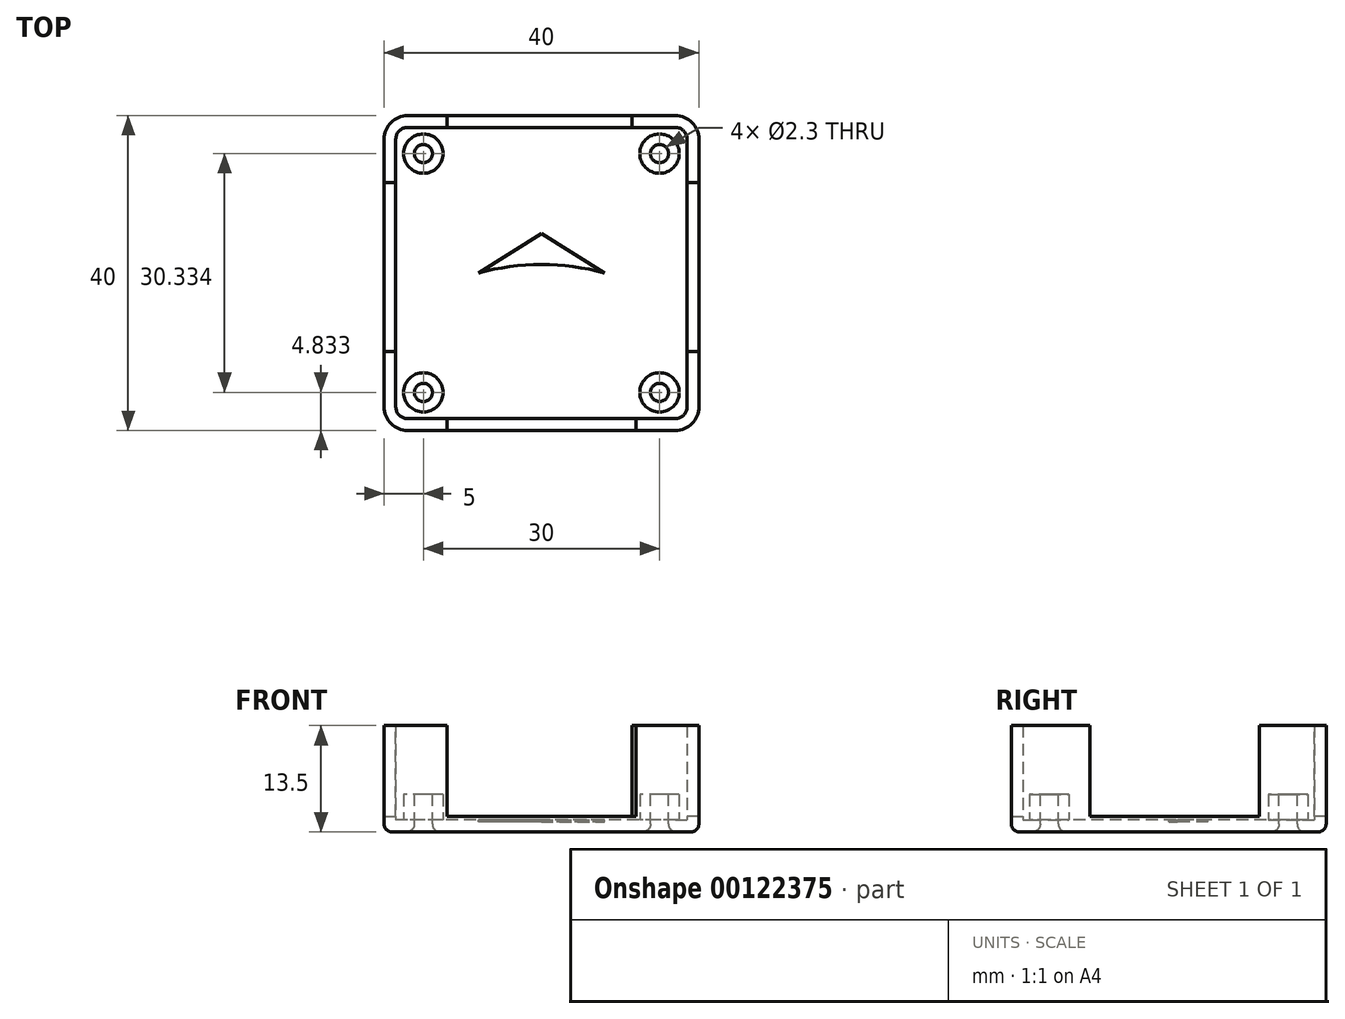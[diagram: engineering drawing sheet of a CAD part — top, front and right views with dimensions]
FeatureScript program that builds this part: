
annotation { "Feature Type Name" : "Feature", "Feature Type Description" : "" }
export const myFeature = defineFeature(function(context is Context, id is Id, definition is map)
    precondition{}
    {
        {
            var Q0;
            Q0=qCreatedBy(makeId("Top.planeOp"),FACE);
            var sketch = newSketch(context, id + "F0", { "sketchPlane" : qUnion([Q0])});
            skLineSegment(sketch, "E0.bottom", {"start": v(20, 20) * mm, "end": v(-20, 20) * mm});
            skLineSegment(sketch, "E0.top", {"start": v(20, -20) * mm, "end": v(-20, -20) * mm});
            skLineSegment(sketch, "E0.left", {"start": v(20, 20) * mm, "end": v(20, -20) * mm});
            skLineSegment(sketch, "E0.right", {"start": v(-20, 20) * mm, "end": v(-20, -20) * mm});
            skPoint(sketch, "E0.middle", {"position": v(0, 0) * mm});
            skSolve(sketch);
        }
        {
            var Q0;
            Q0 = qSketchRegion(id + "F0", true);
            extrude(context, id + "F1", {"entities" : qUnion([Q0]), "depth" : 1.5 * mm});
        }
        {
            var Q0;
            Q0=makeQuery(id+"F1.opExtrude","CAP_FACE",FACE,{"disambiguationData":[OSD([sQuery(id+"F0.wireOp",EDGE,"E0.bottom"),sQuery(id+"F0.wireOp",EDGE,"E0.top"),sQuery(id+"F0.wireOp",EDGE,"E0.left"),sQuery(id+"F0.wireOp",EDGE,"E0.right")])],"isStart":false});
            var sketch = newSketch(context, id + "F2", { "sketchPlane" : qUnion([Q0])});
            skLineSegment(sketch, "E1.0", {"start": v(20, 20) * mm, "end": v(-20, 20) * mm});
            skLineSegment(sketch, "E2.0", {"start": v(-20, 20) * mm, "end": v(-20, -20) * mm});
            skLineSegment(sketch, "E3.0", {"start": v(20, 20) * mm, "end": v(20, -20) * mm});
            skLineSegment(sketch, "E4.0", {"start": v(20, -20) * mm, "end": v(-20, -20) * mm});
            skLineSegment(sketch, "E5.0", {"start": v(18.5, 18.5) * mm, "end": v(-18.5, 18.5) * mm});
            skLineSegment(sketch, "E6.0", {"start": v(-18.5, 18.5) * mm, "end": v(-18.5, -18.5) * mm});
            skLineSegment(sketch, "E7.0", {"start": v(18.5, -18.5) * mm, "end": v(-18.5, -18.5) * mm});
            skLineSegment(sketch, "E8.0", {"start": v(18.5, 18.5) * mm, "end": v(18.5, -18.5) * mm});
            skSolve(sketch);
        }
        {
            var Q0;
            Q0 = qSketchRegion(id + "F2", true);
            extrude(context, id + "F3", {"entities" : qUnion([Q0]), "operationType" : NewBodyOperationType.ADD, "depth" : 12 * mm});
        }
        {
            var Q0;
            Q0=makeQuery(id+"F1.opExtrude","CAP_FACE",FACE,{"disambiguationData":[OSD([sQuery(id+"F0.wireOp",EDGE,"E0.bottom"),sQuery(id+"F0.wireOp",EDGE,"E0.top"),sQuery(id+"F0.wireOp",EDGE,"E0.left"),sQuery(id+"F0.wireOp",EDGE,"E0.right")])],"isStart":false});
            var sketch = newSketch(context, id + "F4", { "sketchPlane" : qUnion([Q0])});
            skLineSegment(sketch, "E9.bottom", {"start": v(15, -15.17) * mm, "end": v(-15, -15.17) * mm, "construction": true});
            skLineSegment(sketch, "E9.top", {"start": v(15, 15.17) * mm, "end": v(-15, 15.17) * mm, "construction": true});
            skLineSegment(sketch, "E9.left", {"start": v(15, -15.17) * mm, "end": v(15, 15.17) * mm, "construction": true});
            skLineSegment(sketch, "E9.right", {"start": v(-15, -15.17) * mm, "end": v(-15, 15.17) * mm, "construction": true});
            skPoint(sketch, "E9.middle", {"position": v(0, 0) * mm});
            skCircle(sketch, "E10", {"center": v(-15, 15.17) * mm, "radius": 2.5 * mm});
            skCircle(sketch, "E11", {"center": v(15, 15.17) * mm, "radius": 2.5 * mm});
            skCircle(sketch, "E12", {"center": v(15, -15.17) * mm, "radius": 2.5 * mm});
            skCircle(sketch, "E13", {"center": v(-15, -15.17) * mm, "radius": 2.5 * mm});
            skSolve(sketch);
        }
        {
            var Q0;
            Q0 = qSketchRegion(id + "F4", true);
            extrude(context, id + "F5", {"entities" : qUnion([Q0]), "operationType" : NewBodyOperationType.ADD, "depth" : 3.25 * mm});
        }
        {
            var Q0;
            Q0=makeQuery(id+"F5.opExtrude","CAP_FACE",FACE,{"disambiguationData":[OSD([sQuery(id+"F4.wireOp",EDGE,"E10")])],"isStart":false});
            var sketch = newSketch(context, id + "F6", { "sketchPlane" : qUnion([Q0])});
            skCircle(sketch, "E14", {"center": v(-15, 15.17) * mm, "radius": 1.15 * mm});
            skCircle(sketch, "E15.0", {"center": v(15, 15.17) * mm, "radius": 2.5 * mm, "construction": true});
            skCircle(sketch, "E16.1", {"center": v(-15, -15.17) * mm, "radius": 2.5 * mm, "construction": true});
            skCircle(sketch, "E16.2", {"center": v(15, -15.17) * mm, "radius": 2.5 * mm, "construction": true});
            skCircle(sketch, "E17", {"center": v(15, 15.17) * mm, "radius": 1.15 * mm});
            skCircle(sketch, "E18", {"center": v(-15, -15.17) * mm, "radius": 1.15 * mm});
            skCircle(sketch, "E19", {"center": v(15, -15.17) * mm, "radius": 1.15 * mm});
            skSolve(sketch);
        }
        {
            var Q0;
            Q0 = qSketchRegion(id + "F6", true);
            extrude(context, id + "F7", {"entities" : qUnion([Q0]), "operationType" : NewBodyOperationType.REMOVE, "endBound" : BoundingType.THROUGH_ALL, "oppositeDirection" : true, "depth" : 25.4 * mm});
        }
        {
            var Q0;
            Q0=makeQuery(id+"F3.opExtrude","CAP_FACE",FACE,{"disambiguationData":[OSD([sQuery(id+"F2.wireOp",EDGE,"E1.0"),sQuery(id+"F2.wireOp",EDGE,"E2.0"),sQuery(id+"F2.wireOp",EDGE,"E3.0"),sQuery(id+"F2.wireOp",EDGE,"E4.0"),sQuery(id+"F2.wireOp",EDGE,"E5.0"),sQuery(id+"F2.wireOp",EDGE,"E6.0"),sQuery(id+"F2.wireOp",EDGE,"E7.0"),sQuery(id+"F2.wireOp",EDGE,"E8.0")])],"isStart":false});
            var sketch = newSketch(context, id + "F8", { "sketchPlane" : qUnion([Q0])});
            skLineSegment(sketch, "E20", {"start": v(-12, 25.4) * mm, "end": v(-12, 11.5) * mm});
            skLineSegment(sketch, "E21", {"start": v(-12, 11.5) * mm, "end": v(-27.13, 11.5) * mm});
            skLineSegment(sketch, "E22", {"start": v(-27.13, 11.5) * mm, "end": v(-27.13, -10) * mm});
            skLineSegment(sketch, "E23", {"start": v(-27.13, -10) * mm, "end": v(-12, -10) * mm});
            skLineSegment(sketch, "E24", {"start": v(-12, -10) * mm, "end": v(-12, -25.4) * mm});
            skLineSegment(sketch, "E25", {"start": v(-12, -25.4) * mm, "end": v(12, -25.4) * mm});
            skLineSegment(sketch, "E26", {"start": v(12, -25.4) * mm, "end": v(12, -10) * mm});
            skLineSegment(sketch, "E27", {"start": v(12, -10) * mm, "end": v(25.4, -10) * mm});
            skLineSegment(sketch, "E28", {"start": v(25.4, -10) * mm, "end": v(25.4, 11.5) * mm});
            skLineSegment(sketch, "E29", {"start": v(25.4, 11.5) * mm, "end": v(11.5, 11.5) * mm});
            skLineSegment(sketch, "E30", {"start": v(11.5, 11.5) * mm, "end": v(11.5, 25.4) * mm});
            skLineSegment(sketch, "E31", {"start": v(11.5, 25.4) * mm, "end": v(-12, 25.4) * mm});
            skSolve(sketch);
        }
        {
            var Q0;
            Q0 = qSketchRegion(id + "F8", true);
            extrude(context, id + "F9", {"entities" : qUnion([Q0]), "operationType" : NewBodyOperationType.REMOVE, "oppositeDirection" : true, "depth" : 11.5 * mm});
        }
        {
            var Q0;
            Q0=makeQuery(id+"F1.opExtrude","CAP_FACE",FACE,{"disambiguationData":[OSD([sQuery(id+"F0.wireOp",EDGE,"E0.bottom"),sQuery(id+"F0.wireOp",EDGE,"E0.top"),sQuery(id+"F0.wireOp",EDGE,"E0.left"),sQuery(id+"F0.wireOp",EDGE,"E0.right")])],"isStart":false});
            var sketch = newSketch(context, id + "F10", { "sketchPlane" : qUnion([Q0])});
            skLineSegment(sketch, "E32", {"start": v(0, 0) * mm, "end": v(0, 10) * mm, "construction": true});
            skLineSegment(sketch, "E33", {"start": v(0, 5) * mm, "end": v(-8, 0) * mm});
            skLineSegment(sketch, "E34", {"start": v(0, 5) * mm, "end": v(8, 0) * mm});
            skArc(sketch, "E35", {"start": v(8, 0) * mm, "mid": v(0, 1.09) * mm, "end": v(-8, 0) * mm});
            skSolve(sketch);
        }
        {
            var Q0;
            Q0 = qSketchRegion(id + "F10", true);
            extrude(context, id + "F11", {"entities" : qUnion([Q0]), "operationType" : NewBodyOperationType.REMOVE, "oppositeDirection" : true, "depth" : .25 * mm});
        }
        {
            var Q0;
            Q0=makeQuery(id+"F1.opExtrude","CAP_FACE",FACE,{"disambiguationData":[OSD([sQuery(id+"F0.wireOp",EDGE,"E0.bottom"),sQuery(id+"F0.wireOp",EDGE,"E0.top"),sQuery(id+"F0.wireOp",EDGE,"E0.left"),sQuery(id+"F0.wireOp",EDGE,"E0.right")])],"isStart":true});
            fillet(context, id + "F12", {"entities" : qUnion([Q0]), "radius" : 1 * mm, "tangentPropagation" : true, "allowEdgeOverflow" : false});
        }
        {
            var Q0;
            Q0=makeQuery(id+"F3.boolean.opBoolean","MERGE",EDGE,{"derivedFrom":[makeQuery(id+"F1.opExtrude","SWEPT_EDGE",EDGE,{"disambiguationData":[OSD([sQuery(id+"F0.wireOp",EDGE,"E0.top"),sQuery(id+"F0.wireOp",EDGE,"E0.left")])]}),makeQuery(id+"F3.opExtrude","SWEPT_EDGE",EDGE,{"disambiguationData":[OSD([sQuery(id+"F2.wireOp",EDGE,"E3.0"),sQuery(id+"F2.wireOp",EDGE,"E4.0")])]})]});
            var Q1;
            Q1=makeQuery(id+"F3.boolean.opBoolean","MERGE",EDGE,{"derivedFrom":[makeQuery(id+"F1.opExtrude","SWEPT_EDGE",EDGE,{"disambiguationData":[OSD([sQuery(id+"F0.wireOp",EDGE,"E0.bottom"),sQuery(id+"F0.wireOp",EDGE,"E0.left")])]}),makeQuery(id+"F3.opExtrude","SWEPT_EDGE",EDGE,{"disambiguationData":[OSD([sQuery(id+"F2.wireOp",EDGE,"E1.0"),sQuery(id+"F2.wireOp",EDGE,"E3.0")])]})]});
            var Q2;
            Q2=makeQuery(id+"F3.boolean.opBoolean","MERGE",EDGE,{"derivedFrom":[makeQuery(id+"F1.opExtrude","SWEPT_EDGE",EDGE,{"disambiguationData":[OSD([sQuery(id+"F0.wireOp",EDGE,"E0.bottom"),sQuery(id+"F0.wireOp",EDGE,"E0.right")])]}),makeQuery(id+"F3.opExtrude","SWEPT_EDGE",EDGE,{"disambiguationData":[OSD([sQuery(id+"F2.wireOp",EDGE,"E1.0"),sQuery(id+"F2.wireOp",EDGE,"E2.0")])]})]});
            var Q3;
            Q3=makeQuery(id+"F3.boolean.opBoolean","MERGE",EDGE,{"derivedFrom":[makeQuery(id+"F1.opExtrude","SWEPT_EDGE",EDGE,{"disambiguationData":[OSD([sQuery(id+"F0.wireOp",EDGE,"E0.top"),sQuery(id+"F0.wireOp",EDGE,"E0.right")])]}),makeQuery(id+"F3.opExtrude","SWEPT_EDGE",EDGE,{"disambiguationData":[OSD([sQuery(id+"F2.wireOp",EDGE,"E2.0"),sQuery(id+"F2.wireOp",EDGE,"E4.0")])]})]});
            fillet(context, id + "F13", {"entities" : qUnion([Q0, Q1, Q2, Q3]), "radius" : 3 * mm, "tangentPropagation" : true, "allowEdgeOverflow" : false});
        }
        {
            var Q0;
            Q0=makeQuery(id+"F3.opExtrude","SWEPT_EDGE",EDGE,{"disambiguationData":[OSD([sQuery(id+"F2.wireOp",EDGE,"E5.0"),sQuery(id+"F2.wireOp",EDGE,"E6.0")])]});
            var Q1;
            Q1=makeQuery(id+"F3.opExtrude","SWEPT_EDGE",EDGE,{"disambiguationData":[OSD([sQuery(id+"F2.wireOp",EDGE,"E5.0"),sQuery(id+"F2.wireOp",EDGE,"E8.0")])]});
            var Q2;
            Q2=makeQuery(id+"F3.opExtrude","SWEPT_EDGE",EDGE,{"disambiguationData":[OSD([sQuery(id+"F2.wireOp",EDGE,"E6.0"),sQuery(id+"F2.wireOp",EDGE,"E7.0")])]});
            var Q3;
            Q3=makeQuery(id+"F3.opExtrude","SWEPT_EDGE",EDGE,{"disambiguationData":[OSD([sQuery(id+"F2.wireOp",EDGE,"E7.0"),sQuery(id+"F2.wireOp",EDGE,"E8.0")])]});
            fillet(context, id + "F14", {"entities" : qUnion([Q0, Q1, Q2, Q3]), "radius" : 1.5 * mm, "tangentPropagation" : true, "allowEdgeOverflow" : false});
        }
    });
